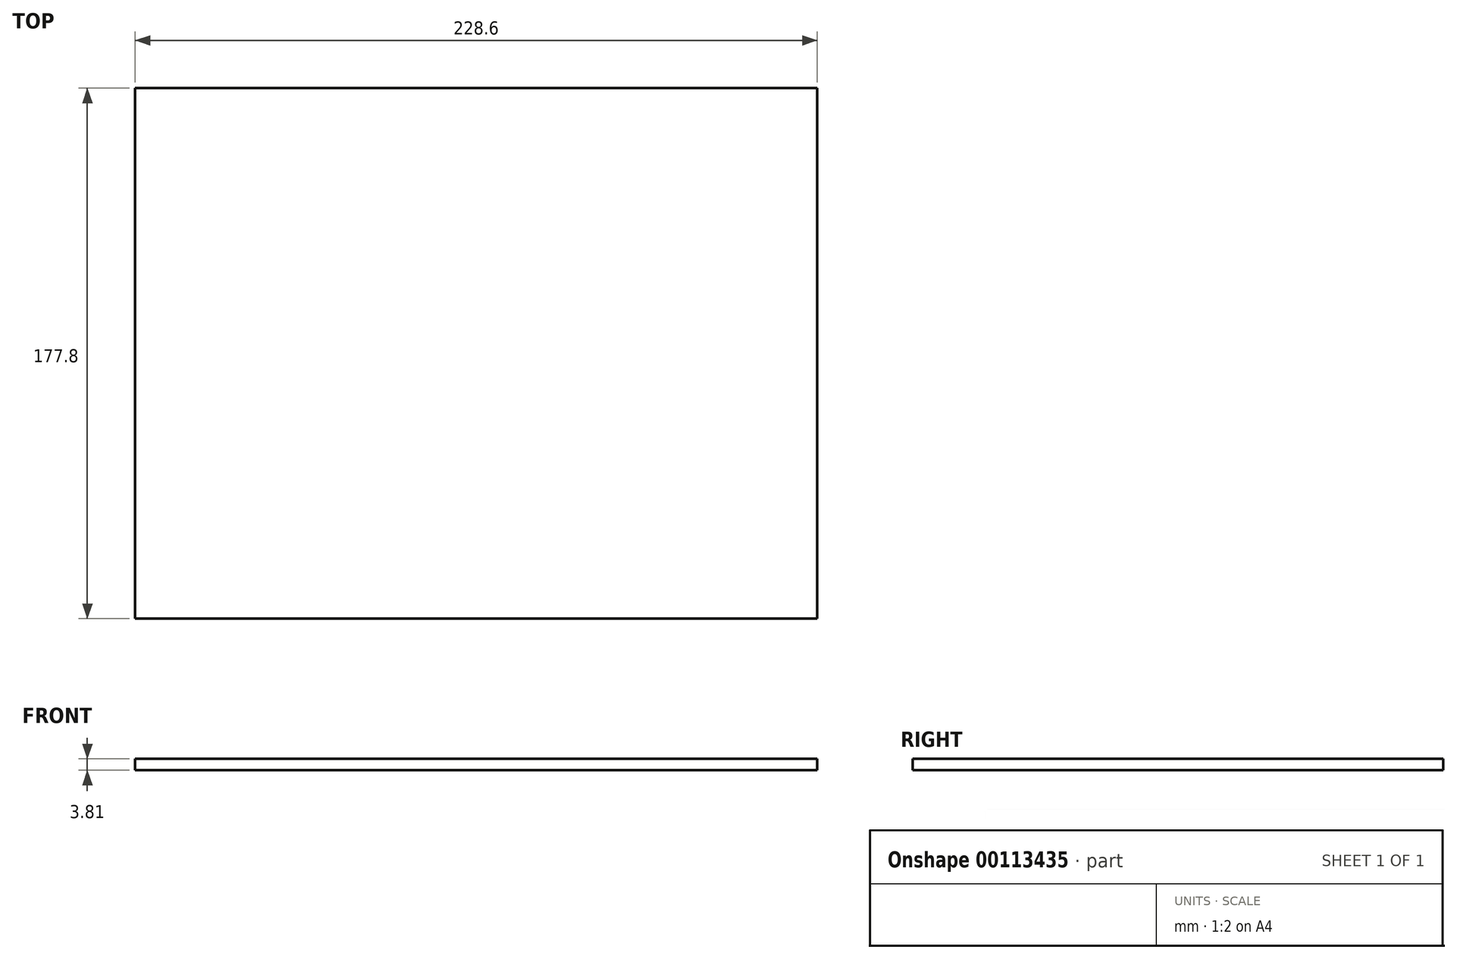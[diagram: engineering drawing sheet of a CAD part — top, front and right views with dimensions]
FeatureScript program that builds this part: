
annotation { "Feature Type Name" : "Feature", "Feature Type Description" : "" }
export const myFeature = defineFeature(function(context is Context, id is Id, definition is map)
    precondition{}
    {
        {
            var Q0;
            Q0=qCreatedBy(makeId("Top.planeOp"),FACE);
            var sketch = newSketch(context, id + "F0", { "sketchPlane" : qUnion([Q0])});
            skLineSegment(sketch, "E0.bottom", {"start": v(-77.04, 108.7) * mm, "end": v(151.56, 108.7) * mm});
            skLineSegment(sketch, "E0.top", {"start": v(-77.04, -69.1) * mm, "end": v(151.56, -69.1) * mm});
            skLineSegment(sketch, "E0.left", {"start": v(-77.04, 108.7) * mm, "end": v(-77.04, -69.1) * mm});
            skLineSegment(sketch, "E0.right", {"start": v(151.56, 108.7) * mm, "end": v(151.56, -69.1) * mm});
            skSolve(sketch);
        }
        {
            var Q0;
            Q0 = qSketchRegion(id + "F0", true);
            var Q1;
            Q1=makeQuery(id+"F0.imprint","IMPRINT",FACE,{"disambiguationData":[TD([[makeQuery(id+"F0.imprint","IMPRINT",EDGE,{"derivedFrom":sQuery(id+"F0.wireOp",EDGE,"E0.bottom")}),-1.0]])]});
            extrude(context, id + "F1", {"entities" : qUnion([Q0, Q1]), "depth" : 3.8 * mm});
        }
    });
